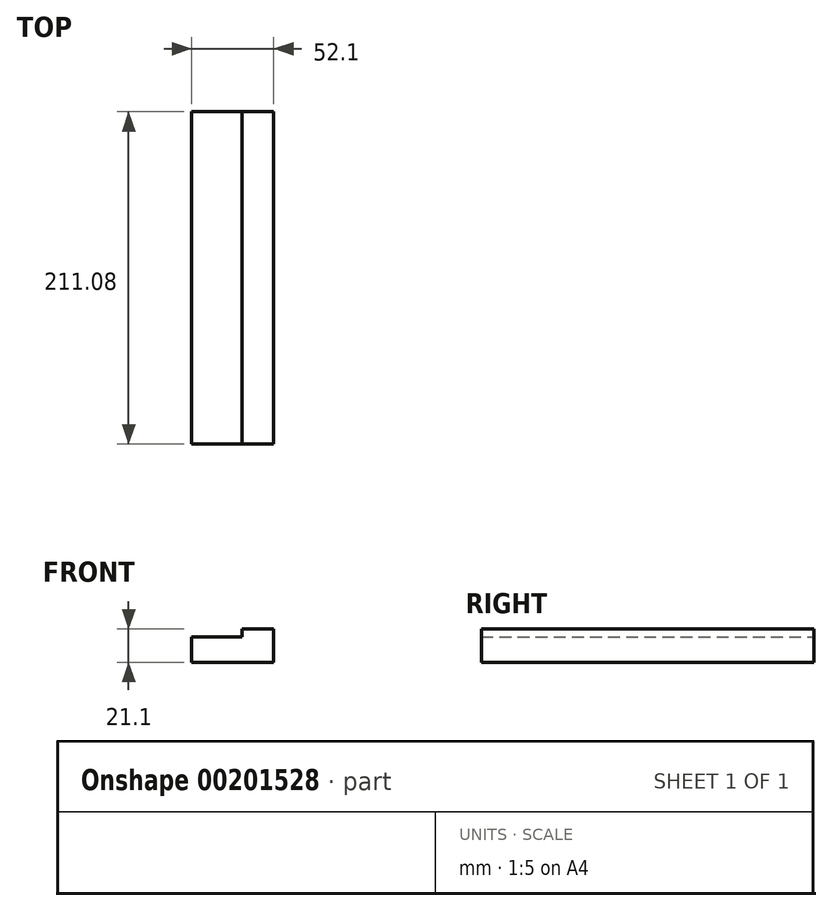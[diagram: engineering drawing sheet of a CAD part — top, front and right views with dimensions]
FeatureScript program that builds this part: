
annotation { "Feature Type Name" : "Feature", "Feature Type Description" : "" }
export const myFeature = defineFeature(function(context is Context, id is Id, definition is map)
    precondition{}
    {
        {
            var Q0;
            Q0=qCreatedBy(makeId("Front.planeOp"),FACE);
            var sketch = newSketch(context, id + "F0", { "sketchPlane" : qUnion([Q0])});
            skLineSegment(sketch, "E0.top", {"start": v(-26.05, 10.55) * mm, "end": v(26.05, 10.55) * mm});
            skLineSegment(sketch, "E0.left", {"start": v(-26.05, -10.55) * mm, "end": v(-26.05, 10.55) * mm});
            skLineSegment(sketch, "E0.right", {"start": v(26.05, -10.55) * mm, "end": v(26.05, 10.55) * mm});
            skLineSegment(sketch, "E1", {"start": v(-26.05, -10.55) * mm, "end": v(26.05, -10.55) * mm});
            skLineSegment(sketch, "E2", {"start": v(-26.05, 0) * mm, "end": v(0, 0) * mm, "construction": true});
            skLineSegment(sketch, "E3", {"start": v(0, 0) * mm, "end": v(0, 10.55) * mm, "construction": true});
            skSolve(sketch);
        }
        {
            var Q0;
            Q0=makeQuery(id+"F0.imprint","IMPRINT",FACE,{"disambiguationData":[TD([[makeQuery(id+"F0.imprint","IMPRINT",EDGE,{"derivedFrom":sQuery(id+"F0.wireOp",EDGE,"E0.top")}),-1.0]])]});
            extrude(context, id + "F1", {"entities" : qUnion([Q0]), "endBound" : BoundingType.SYMMETRIC, "depth" : 211.07 * mm});
        }
        {
            var Q0;
            Q0=makeQuery(id+"F1.opExtrude","SWEPT_FACE",FACE,{"disambiguationData":[OSD([sQuery(id+"F0.wireOp",EDGE,"E0.top")])]});
            var sketch = newSketch(context, id + "F2", { "sketchPlane" : qUnion([Q0])});
            skLineSegment(sketch, "E4.bottom", {"start": v(5.9, 105.54) * mm, "end": v(-26.05, 105.54) * mm});
            skLineSegment(sketch, "E4.top", {"start": v(5.9, -105.54) * mm, "end": v(-26.05, -105.54) * mm});
            skLineSegment(sketch, "E4.left", {"start": v(5.9, 105.54) * mm, "end": v(5.9, -105.54) * mm});
            skLineSegment(sketch, "E4.right", {"start": v(-26.05, 105.54) * mm, "end": v(-26.05, -105.54) * mm});
            skSolve(sketch);
        }
        {
            var Q0;
            Q0=makeQuery(id+"F2.imprint","IMPRINT",FACE,{"disambiguationData":[TD([[makeQuery(id+"F2.imprint","IMPRINT",EDGE,{"derivedFrom":sQuery(id+"F2.wireOp",EDGE,"E4.bottom")}),-1.0]])]});
            extrude(context, id + "F3", {"entities" : qUnion([Q0]), "operationType" : NewBodyOperationType.REMOVE, "oppositeDirection" : true, "depth" : 5.08 * mm});
        }
    });
